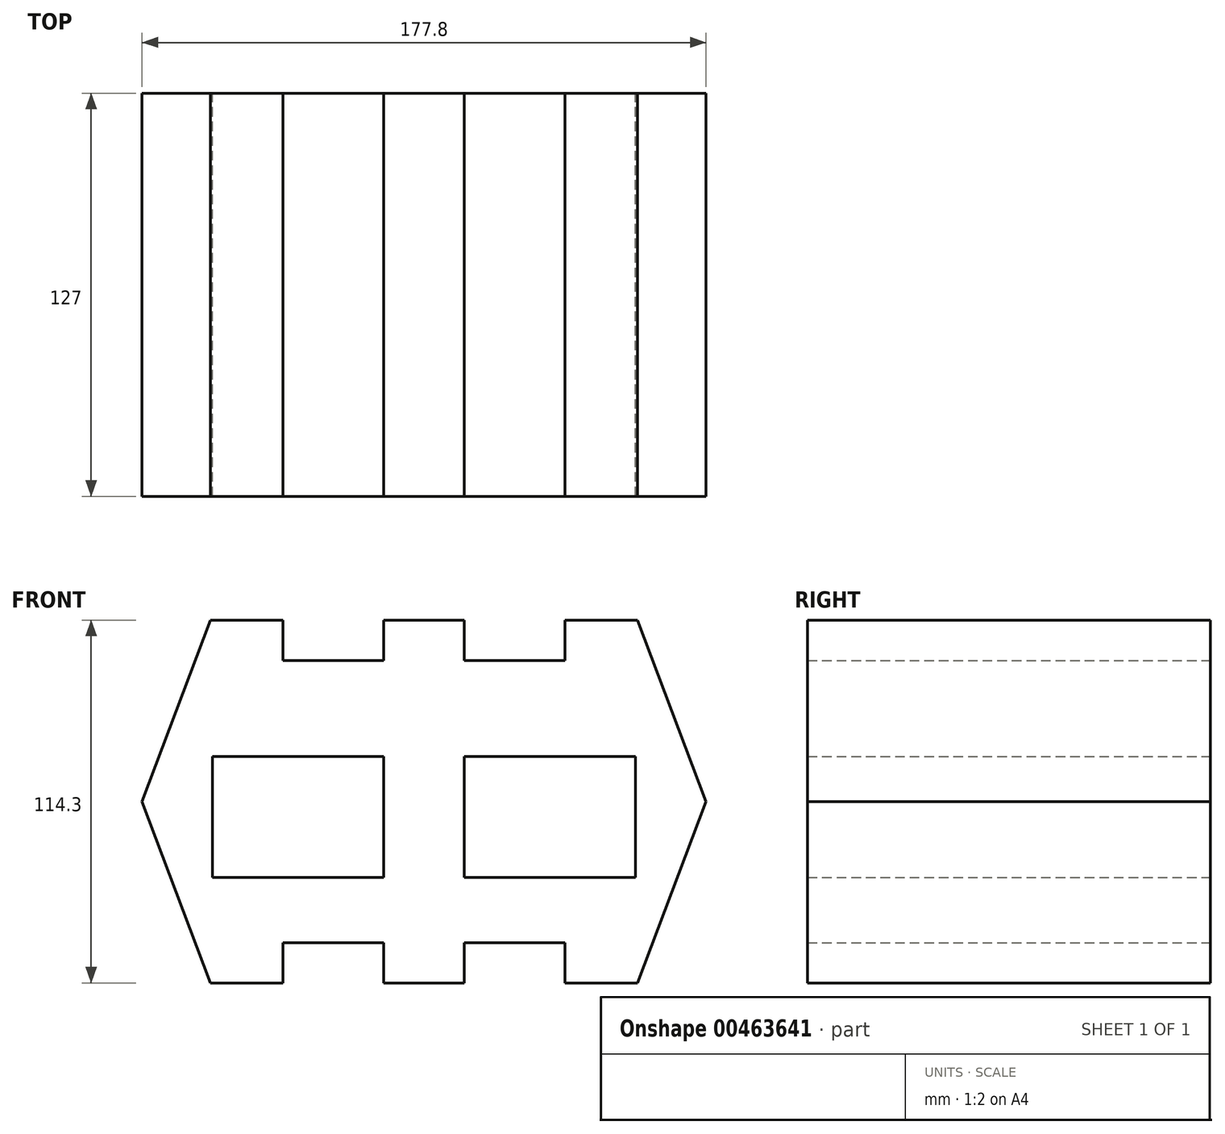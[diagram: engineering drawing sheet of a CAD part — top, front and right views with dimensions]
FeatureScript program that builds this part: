
annotation { "Feature Type Name" : "Feature", "Feature Type Description" : "" }
export const myFeature = defineFeature(function(context is Context, id is Id, definition is map)
    precondition{}
    {
        {
            var Q0;
            Q0=qCreatedBy(makeId("Front.planeOp"),FACE);
            var sketch = newSketch(context, id + "F0", { "sketchPlane" : qUnion([Q0])});
            skLineSegment(sketch, "E0", {"start": v(0, 76.2) * mm, "end": v(12.7, 76.2) * mm});
            skLineSegment(sketch, "E1", {"start": v(12.7, 76.2) * mm, "end": v(12.7, 63.5) * mm});
            skLineSegment(sketch, "E2", {"start": v(12.7, 63.5) * mm, "end": v(44.45, 63.5) * mm});
            skLineSegment(sketch, "E3", {"start": v(44.45, 63.5) * mm, "end": v(44.45, 76.2) * mm});
            skLineSegment(sketch, "E4", {"start": v(44.45, 76.2) * mm, "end": v(67.3, 76.2) * mm});
            skPoint(sketch, "E5.end.orphan", {"position": v(-91.46, 17.16) * mm});
            skPoint(sketch, "E6.end.orphan", {"position": v(-12.7, 45.9) * mm});
            skLineSegment(sketch, "E7", {"start": v(0, -38.1) * mm, "end": v(12.7, -38.1) * mm});
            skLineSegment(sketch, "E8", {"start": v(12.7, -38.1) * mm, "end": v(12.7, -25.4) * mm});
            skLineSegment(sketch, "E9", {"start": v(12.7, -25.4) * mm, "end": v(44.45, -25.4) * mm});
            skLineSegment(sketch, "E10", {"start": v(44.45, -25.4) * mm, "end": v(44.45, -38.1) * mm});
            skLineSegment(sketch, "E11", {"start": v(44.45, -38.1) * mm, "end": v(67.31, -38.1) * mm});
            skLineSegment(sketch, "E12", {"start": v(67.3, 76.2) * mm, "end": v(88.9, 19.05) * mm});
            skLineSegment(sketch, "E13", {"start": v(88.9, 19.05) * mm, "end": v(67.31, -38.1) * mm});
            skLineSegment(sketch, "E14", {"start": v(12.7, 33.26) * mm, "end": v(66.68, 33.26) * mm});
            skLineSegment(sketch, "E15", {"start": v(66.68, 33.26) * mm, "end": v(66.68, -4.84) * mm});
            skLineSegment(sketch, "E16", {"start": v(66.68, -4.84) * mm, "end": v(12.7, -4.84) * mm});
            skLineSegment(sketch, "E17", {"start": v(12.7, -4.84) * mm, "end": v(12.7, 33.26) * mm});
            skLineSegment(sketch, "E18.MirrorCS", {"start": v(0, 76.2) * mm, "end": v(-12.7, 76.2) * mm});
            skLineSegment(sketch, "E19.MirrorCS", {"start": v(-44.45, 63.5) * mm, "end": v(-44.45, 76.2) * mm});
            skLineSegment(sketch, "E20.MirrorCS", {"start": v(-44.45, 76.2) * mm, "end": v(-67.3, 76.2) * mm});
            skLineSegment(sketch, "E21.MirrorCS", {"start": v(-67.3, 76.2) * mm, "end": v(-88.9, 19.05) * mm});
            skLineSegment(sketch, "E22.MirrorCS", {"start": v(-88.9, 19.05) * mm, "end": v(-67.31, -38.1) * mm});
            skLineSegment(sketch, "E23.MirrorCS", {"start": v(-44.45, -38.1) * mm, "end": v(-67.31, -38.1) * mm});
            skLineSegment(sketch, "E24.MirrorCS", {"start": v(-44.45, -25.4) * mm, "end": v(-44.45, -38.1) * mm});
            skLineSegment(sketch, "E25.MirrorCS", {"start": v(-12.7, -25.4) * mm, "end": v(-44.45, -25.4) * mm});
            skLineSegment(sketch, "E26.MirrorCS", {"start": v(-12.7, -38.1) * mm, "end": v(-12.7, -25.4) * mm});
            skLineSegment(sketch, "E27.MirrorCS", {"start": v(0, -38.1) * mm, "end": v(-12.7, -38.1) * mm});
            skLineSegment(sketch, "E28.MirrorCS", {"start": v(-12.7, 33.26) * mm, "end": v(-66.68, 33.26) * mm});
            skLineSegment(sketch, "E29.MirrorCS", {"start": v(-12.7, -4.84) * mm, "end": v(-12.7, 33.26) * mm});
            skLineSegment(sketch, "E30.MirrorCS", {"start": v(-66.68, -4.84) * mm, "end": v(-12.7, -4.84) * mm});
            skLineSegment(sketch, "E31.MirrorCS", {"start": v(-66.68, 33.26) * mm, "end": v(-66.68, -4.84) * mm});
            skLineSegment(sketch, "E32", {"start": v(-12.7, 63.5) * mm, "end": v(-44.45, 63.5) * mm});
            skLineSegment(sketch, "E33", {"start": v(-12.7, 76.2) * mm, "end": v(-12.7, 63.5) * mm});
            skSolve(sketch);
        }
        {
            var Q0;
            Q0 = qSketchRegion(id + "F0", true);
            extrude(context, id + "F1", {"entities" : qUnion([Q0]), "depth" : 127 * mm});
        }
    });
